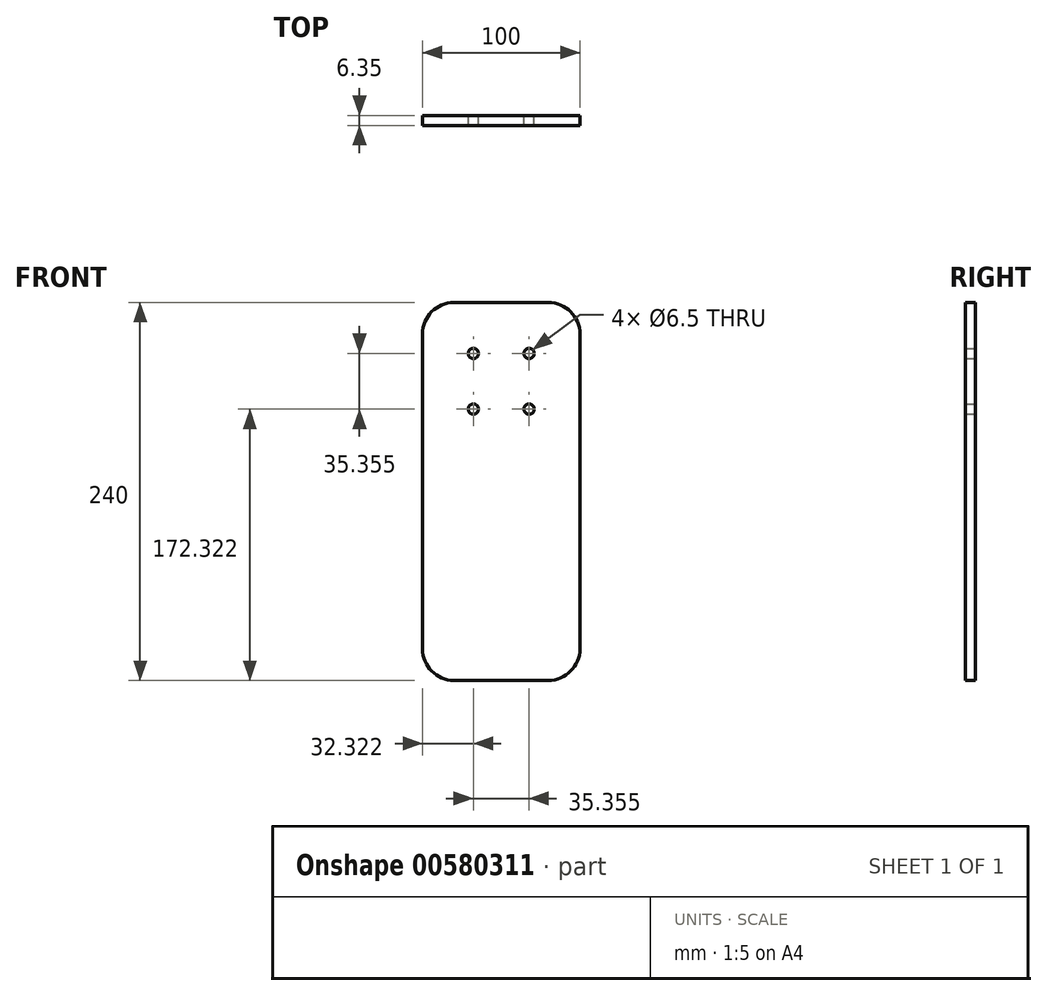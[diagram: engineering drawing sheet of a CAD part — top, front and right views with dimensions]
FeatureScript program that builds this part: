
annotation { "Feature Type Name" : "Feature", "Feature Type Description" : "" }
export const myFeature = defineFeature(function(context is Context, id is Id, definition is map)
    precondition{}
    {
        {
            var Q0;
            Q0=qCreatedBy(makeId("Front.planeOp"),FACE);
            var sketch = newSketch(context, id + "F0", { "sketchPlane" : qUnion([Q0])});
            skLineSegment(sketch, "E0.bottom", {"start": v(-30, 50) * mm, "end": v(30, 50) * mm});
            skLineSegment(sketch, "E0.top", {"start": v(-30, -190) * mm, "end": v(30, -190) * mm});
            skLineSegment(sketch, "E0.left", {"start": v(-50, 30) * mm, "end": v(-50, -170) * mm});
            skLineSegment(sketch, "E0.right", {"start": v(50, 30) * mm, "end": v(50, -170) * mm});
            skLineSegment(sketch, "E1", {"start": v(0, 50) * mm, "end": v(0, -190) * mm, "construction": true});
            skCircle(sketch, "E2", {"center": v(0, 0) * mm, "radius": 25 * mm, "construction": true});
            skCircle(sketch, "E3", {"center": v(0, 0) * mm, "radius": 37.5 * mm, "construction": true});
            skCircle(sketch, "E4", {"center": v(0, -150) * mm, "radius": 25.75 * mm, "construction": true});
            skPoint(sketch, "E5.visualSharp", {"position": v(-50, 50) * mm});
            skArc(sketch, "E5.filletArc", {"start": v(-30, 50) * mm, "mid": v(-44.14, 44.14) * mm, "end": v(-50, 30) * mm});
            skPoint(sketch, "E6.visualSharp", {"position": v(50, 50) * mm});
            skArc(sketch, "E6.filletArc", {"start": v(50, 30) * mm, "mid": v(44.14, 44.14) * mm, "end": v(30, 50) * mm});
            skPoint(sketch, "E7.visualSharp", {"position": v(50, -190) * mm});
            skArc(sketch, "E7.filletArc", {"start": v(30, -190) * mm, "mid": v(44.14, -184.14) * mm, "end": v(50, -170) * mm});
            skPoint(sketch, "E8.visualSharp", {"position": v(-50, -190) * mm});
            skArc(sketch, "E8.filletArc", {"start": v(-50, -170) * mm, "mid": v(-44.14, -184.14) * mm, "end": v(-30, -190) * mm});
            skCircle(sketch, "E9", {"center": v(17.68, 17.68) * mm, "radius": 3.25 * mm});
            skLineSegment(sketch, "E10", {"start": v(17.68, 17.68) * mm, "end": v(0, 0) * mm, "construction": true});
            skCircle(sketch, "E11.1.0", {"center": v(-17.68, 17.68) * mm, "radius": 3.25 * mm});
            skCircle(sketch, "E11.2.0", {"center": v(-17.68, -17.68) * mm, "radius": 3.25 * mm});
            skCircle(sketch, "E11.3.0", {"center": v(17.68, -17.68) * mm, "radius": 3.25 * mm});
            skSolve(sketch);
        }
        {
            var Q0;
            Q0 = qSketchRegion(id + "F0", true);
            extrude(context, id + "F1", {"entities" : qUnion([Q0]), "depth" : 6.35 * mm, "offsetDistance" : 25 * mm});
        }
    });
